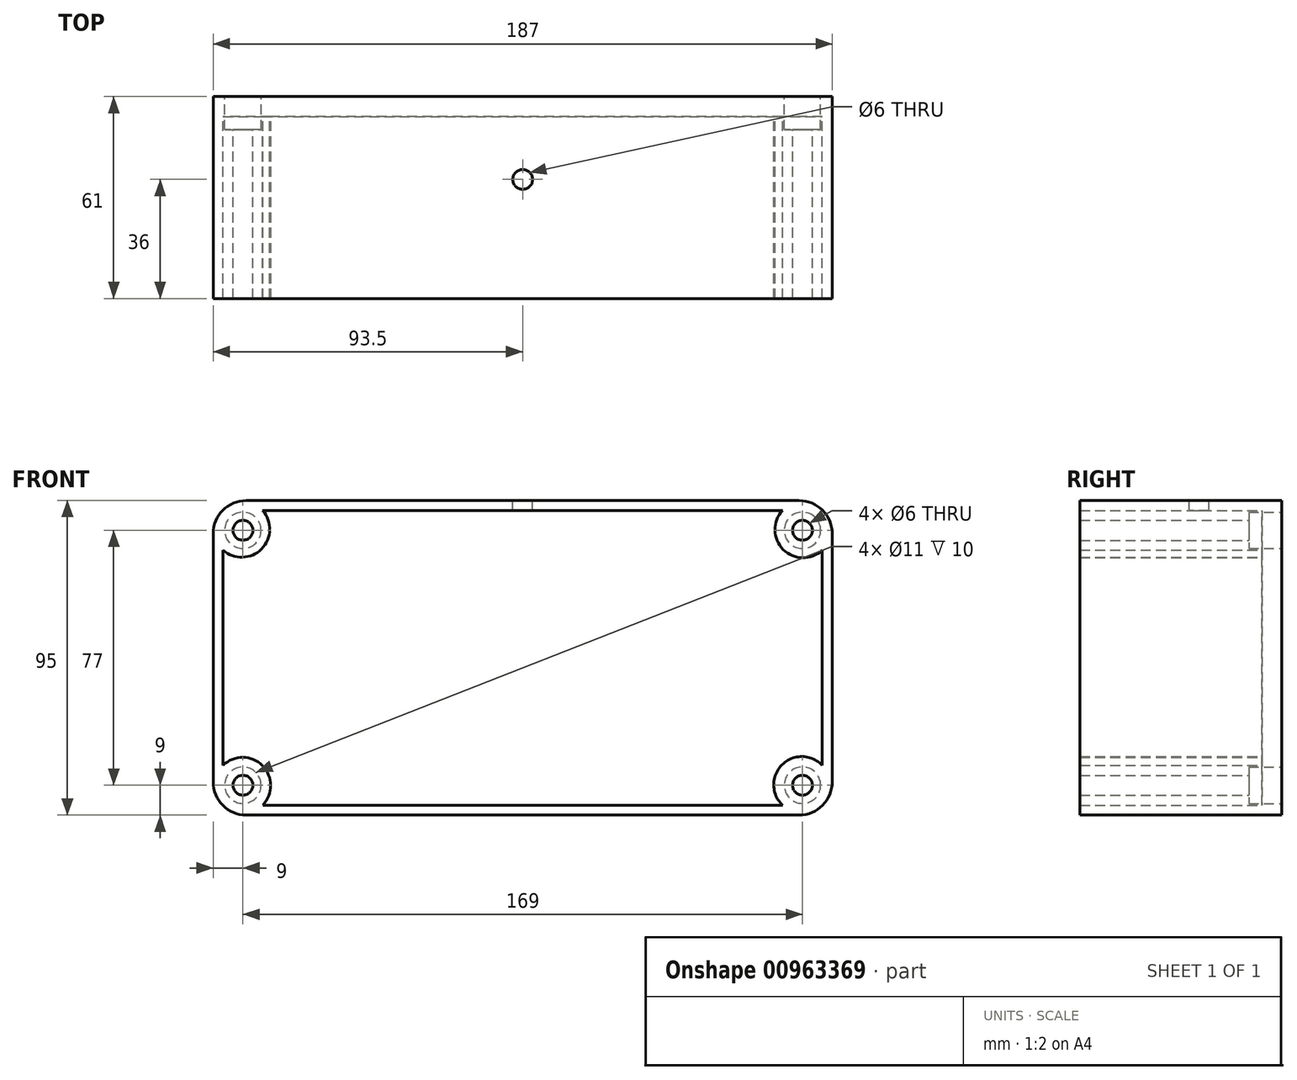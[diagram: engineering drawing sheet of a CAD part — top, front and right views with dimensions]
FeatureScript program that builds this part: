
annotation { "Feature Type Name" : "Feature", "Feature Type Description" : "" }
export const myFeature = defineFeature(function(context is Context, id is Id, definition is map)
    precondition{}
    {
        {
            var Q0;
            Q0=qCreatedBy(makeId("Front.planeOp"),FACE);
            var sketch = newSketch(context, id + "F0", { "sketchPlane" : qUnion([Q0])});
            skLineSegment(sketch, "E0.bottom", {"start": v(68.5, 22.5) * mm, "end": v(-68.5, 22.5) * mm, "construction": true});
            skLineSegment(sketch, "E0.top", {"start": v(68.5, -22.5) * mm, "end": v(-68.5, -22.5) * mm, "construction": true});
            skLineSegment(sketch, "E0.left", {"start": v(68.5, 22.5) * mm, "end": v(68.5, -22.5) * mm, "construction": true});
            skLineSegment(sketch, "E0.right", {"start": v(-68.5, 22.5) * mm, "end": v(-68.5, -22.5) * mm, "construction": true});
            skPoint(sketch, "E0.middle", {"position": v(0, 0) * mm});
            skLineSegment(sketch, "E1.bottom", {"start": v(93.5, 47.5) * mm, "end": v(-93.5, 47.5) * mm});
            skLineSegment(sketch, "E1.top", {"start": v(93.5, -47.5) * mm, "end": v(-93.5, -47.5) * mm});
            skLineSegment(sketch, "E1.left", {"start": v(93.5, 47.5) * mm, "end": v(93.5, -47.5) * mm});
            skLineSegment(sketch, "E1.right", {"start": v(-93.5, 47.5) * mm, "end": v(-93.5, -47.5) * mm});
            skCircle(sketch, "E2", {"center": v(-84.5, 38.5) * mm, "radius": 3 * mm});
            skCircle(sketch, "E3", {"center": v(84.5, 38.5) * mm, "radius": 3 * mm});
            skCircle(sketch, "E4", {"center": v(84.5, -38.5) * mm, "radius": 3 * mm});
            skCircle(sketch, "E5", {"center": v(-84.5, -38.5) * mm, "radius": 3 * mm});
            skLineSegment(sketch, "E6.bottom", {"start": v(84.5, 38.5) * mm, "end": v(-84.5, 38.5) * mm, "construction": true});
            skLineSegment(sketch, "E6.top", {"start": v(84.5, -38.5) * mm, "end": v(-84.5, -38.5) * mm, "construction": true});
            skLineSegment(sketch, "E6.left", {"start": v(84.5, 38.5) * mm, "end": v(84.5, -38.5) * mm, "construction": true});
            skLineSegment(sketch, "E6.right", {"start": v(-84.5, 38.5) * mm, "end": v(-84.5, -38.5) * mm, "construction": true});
            skLineSegment(sketch, "E7.bottom", {"start": v(5.12, 36.5) * mm, "end": v(-5.12, 36.5) * mm, "construction": true});
            skLineSegment(sketch, "E7.top", {"start": v(5.12, 33.5) * mm, "end": v(-5.12, 33.5) * mm, "construction": true});
            skLineSegment(sketch, "E7.left", {"start": v(5.12, 36.5) * mm, "end": v(5.12, 33.5) * mm, "construction": true});
            skLineSegment(sketch, "E7.right", {"start": v(-5.12, 36.5) * mm, "end": v(-5.12, 33.5) * mm, "construction": true});
            skPoint(sketch, "E7.middle", {"position": v(0, 35) * mm});
            skPoint(sketch, "E7.middle.positionSnap0", {"position": v(0, 38.5) * mm});
            skPoint(sketch, "E7.centerSnap0", {"position": v(0, 38.5) * mm});
            skCircle(sketch, "E8", {"center": v(49.83, 35) * mm, "radius": 3 * mm, "construction": true});
            skLineSegment(sketch, "E9.bottom", {"start": v(12.5, 27.5) * mm, "end": v(-12.5, 27.5) * mm, "construction": true});
            skLineSegment(sketch, "E9.top", {"start": v(12.5, 17.5) * mm, "end": v(-12.5, 17.5) * mm, "construction": true});
            skLineSegment(sketch, "E9.left", {"start": v(12.5, 27.5) * mm, "end": v(12.5, 17.5) * mm, "construction": true});
            skLineSegment(sketch, "E9.right", {"start": v(-12.5, 27.5) * mm, "end": v(-12.5, 17.5) * mm, "construction": true});
            skPoint(sketch, "E9.middle", {"position": v(0, 22.5) * mm});
            skSolve(sketch);
        }
        {
            var Q0;
            Q0=qSketchRegion(id+"F0",true);
            extrude(context, id + "F1", {"entities" : qUnion([Q0]), "depth" : 6 * mm, "offsetDistance" : 25 * mm});
        }
        {
            var Q0;
            Q0=makeQuery(id+"F1.opExtrude","CAP_FACE",FACE,{"disambiguationData":[OSD([sQuery(id+"F0.wireOp",EDGE,"E1.bottom"),sQuery(id+"F0.wireOp",EDGE,"E1.top"),sQuery(id+"F0.wireOp",EDGE,"E1.left"),sQuery(id+"F0.wireOp",EDGE,"E1.right"),sQuery(id+"F0.wireOp",EDGE,"E2"),sQuery(id+"F0.wireOp",EDGE,"E3"),sQuery(id+"F0.wireOp",EDGE,"E4"),sQuery(id+"F0.wireOp",EDGE,"E5")])],"isStart":false});
            var sketch = newSketch(context, id + "F2", { "sketchPlane" : qUnion([Q0])});
            skLineSegment(sketch, "E10.bottom", {"start": v(93.5, 47.5) * mm, "end": v(-93.5, 47.5) * mm});
            skLineSegment(sketch, "E10.top", {"start": v(93.5, -47.5) * mm, "end": v(-93.5, -47.5) * mm});
            skLineSegment(sketch, "E10.left", {"start": v(93.5, 47.5) * mm, "end": v(93.5, -47.5) * mm});
            skLineSegment(sketch, "E10.right", {"start": v(-93.5, 47.5) * mm, "end": v(-93.5, -47.5) * mm});
            skPoint(sketch, "E10.middle", {"position": v(0, 0) * mm});
            skLineSegment(sketch, "E11.bottom", {"start": v(90.5, 44.5) * mm, "end": v(-90.5, 44.5) * mm, "construction": true});
            skLineSegment(sketch, "E11.top", {"start": v(90.5, -44.5) * mm, "end": v(-90.5, -44.5) * mm, "construction": true});
            skLineSegment(sketch, "E11.left", {"start": v(90.5, 44.5) * mm, "end": v(90.5, -44.5) * mm, "construction": true});
            skLineSegment(sketch, "E11.right", {"start": v(-90.5, 44.5) * mm, "end": v(-90.5, -44.5) * mm, "construction": true});
            skLineSegment(sketch, "E12", {"start": v(90.5, 32.5) * mm, "end": v(90.5, -32.49) * mm});
            skLineSegment(sketch, "E13", {"start": v(78.48, -44.5) * mm, "end": v(-78.48, -44.5) * mm});
            skLineSegment(sketch, "E14", {"start": v(-90.5, -32.48) * mm, "end": v(-90.5, 32.48) * mm});
            skLineSegment(sketch, "E15", {"start": v(-78.53, 44.5) * mm, "end": v(78.48, 44.5) * mm});
            skArc(sketch, "E16", {"start": v(-78.48, -44.5) * mm, "mid": v(-78.6, -32.6) * mm, "end": v(-90.5, -32.48) * mm});
            skArc(sketch, "E17", {"start": v(90.5, -32.49) * mm, "mid": v(78.32, -32.32) * mm, "end": v(78.48, -44.5) * mm});
            skArc(sketch, "E18", {"start": v(78.48, 44.5) * mm, "mid": v(78.69, 32.69) * mm, "end": v(90.5, 32.5) * mm});
            skArc(sketch, "E19", {"start": v(-90.5, 32.48) * mm, "mid": v(-78.87, 32.87) * mm, "end": v(-78.53, 44.5) * mm});
            skCircle(sketch, "E20", {"center": v(-84.5, 38.5) * mm, "radius": 3 * mm});
            skCircle(sketch, "E21", {"center": v(84.5, 38.5) * mm, "radius": 3 * mm});
            skCircle(sketch, "E22", {"center": v(84.5, -38.5) * mm, "radius": 3 * mm});
            skCircle(sketch, "E23", {"center": v(-84.5, -38.5) * mm, "radius": 3 * mm});
            skSolve(sketch);
        }
        {
            var Q0;
            Q0 = qSketchRegion(id + "F2", true);
            extrude(context, id + "F3", {"entities" : qUnion([Q0]), "operationType" : NewBodyOperationType.ADD, "depth" : 55 * mm, "offsetDistance" : 25 * mm});
        }
        {
            var Q0;
            Q0=makeQuery(id+"F3.boolean.opBoolean","MERGE",EDGE,{"derivedFrom":[makeQuery(id+"F1.opExtrude","SWEPT_EDGE",EDGE,{"disambiguationData":[OSD([sQuery(id+"F0.wireOp",EDGE,"E1.top"),sQuery(id+"F0.wireOp",EDGE,"E1.right")])]}),makeQuery(id+"F3.opExtrude","SWEPT_EDGE",EDGE,{"disambiguationData":[OSD([sQuery(id+"F2.wireOp",EDGE,"E10.top"),sQuery(id+"F2.wireOp",EDGE,"E10.right")])]})]});
            var Q1;
            Q1=makeQuery(id+"F3.boolean.opBoolean","MERGE",EDGE,{"derivedFrom":[makeQuery(id+"F1.opExtrude","SWEPT_EDGE",EDGE,{"disambiguationData":[OSD([sQuery(id+"F0.wireOp",EDGE,"E1.bottom"),sQuery(id+"F0.wireOp",EDGE,"E1.right")])]}),makeQuery(id+"F3.opExtrude","SWEPT_EDGE",EDGE,{"disambiguationData":[OSD([sQuery(id+"F2.wireOp",EDGE,"E10.bottom"),sQuery(id+"F2.wireOp",EDGE,"E10.right")])]})]});
            var Q2;
            Q2=makeQuery(id+"F3.boolean.opBoolean","MERGE",EDGE,{"derivedFrom":[makeQuery(id+"F1.opExtrude","SWEPT_EDGE",EDGE,{"disambiguationData":[OSD([sQuery(id+"F0.wireOp",EDGE,"E1.bottom"),sQuery(id+"F0.wireOp",EDGE,"E1.left")])]}),makeQuery(id+"F3.opExtrude","SWEPT_EDGE",EDGE,{"disambiguationData":[OSD([sQuery(id+"F2.wireOp",EDGE,"E10.bottom"),sQuery(id+"F2.wireOp",EDGE,"E10.left")])]})]});
            var Q3;
            Q3=makeQuery(id+"F3.boolean.opBoolean","MERGE",EDGE,{"derivedFrom":[makeQuery(id+"F1.opExtrude","SWEPT_EDGE",EDGE,{"disambiguationData":[OSD([sQuery(id+"F0.wireOp",EDGE,"E1.top"),sQuery(id+"F0.wireOp",EDGE,"E1.left")])]}),makeQuery(id+"F3.opExtrude","SWEPT_EDGE",EDGE,{"disambiguationData":[OSD([sQuery(id+"F2.wireOp",EDGE,"E10.top"),sQuery(id+"F2.wireOp",EDGE,"E10.left")])]})]});
            fillet(context, id + "F4", {"entities" : qUnion([Q0, Q1, Q2, Q3]), "radius" : 10 * mm, "tangentPropagation" : true, "allowEdgeOverflow" : false});
        }
        {
            var Q0;
            Q0=makeQuery(id+"F1.opExtrude","CAP_FACE",FACE,{"disambiguationData":[OSD([sQuery(id+"F0.wireOp",EDGE,"E1.bottom"),sQuery(id+"F0.wireOp",EDGE,"E1.top"),sQuery(id+"F0.wireOp",EDGE,"E1.left"),sQuery(id+"F0.wireOp",EDGE,"E1.right"),sQuery(id+"F0.wireOp",EDGE,"E2"),sQuery(id+"F0.wireOp",EDGE,"E3"),sQuery(id+"F0.wireOp",EDGE,"E4"),sQuery(id+"F0.wireOp",EDGE,"E5")])],"isStart":true});
            var sketch = newSketch(context, id + "F5", { "sketchPlane" : qUnion([Q0])});
            skCircle(sketch, "E24", {"center": v(-84.5, 38.5) * mm, "radius": 5.5 * mm});
            skCircle(sketch, "E25", {"center": v(-84.5, -38.5) * mm, "radius": 5.5 * mm});
            skCircle(sketch, "E26", {"center": v(84.5, -38.5) * mm, "radius": 5.5 * mm});
            skCircle(sketch, "E27", {"center": v(84.5, 38.5) * mm, "radius": 5.5 * mm});
            skSolve(sketch);
        }
        {
            var Q0;
            Q0 = qSketchRegion(id + "F5", true);
            extrude(context, id + "F6", {"entities" : qUnion([Q0]), "operationType" : NewBodyOperationType.REMOVE, "oppositeDirection" : true, "depth" : 10 * mm, "offsetDistance" : 25 * mm});
        }
        {
            var Q0;
            Q0=makeQuery(id+"F3.boolean.opBoolean","MERGE",FACE,{"derivedFrom":[makeQuery(id+"F1.opExtrude","SWEPT_FACE",FACE,{"disambiguationData":[OSD([sQuery(id+"F0.wireOp",EDGE,"E1.bottom")])]}),makeQuery(id+"F3.opExtrude","SWEPT_FACE",FACE,{"disambiguationData":[OSD([sQuery(id+"F2.wireOp",EDGE,"E10.bottom")])]})]});
            var sketch = newSketch(context, id + "F7", { "sketchPlane" : qUnion([Q0])});
            skCircle(sketch, "E28", {"center": v(0, -25) * mm, "radius": 3 * mm});
            skSolve(sketch);
        }
        {
            var Q0;
            Q0 = qSketchRegion(id + "F7", true);
            extrude(context, id + "F8", {"entities" : qUnion([Q0]), "operationType" : NewBodyOperationType.REMOVE, "oppositeDirection" : true, "depth" : 25 * mm, "offsetDistance" : 25 * mm});
        }
    });
